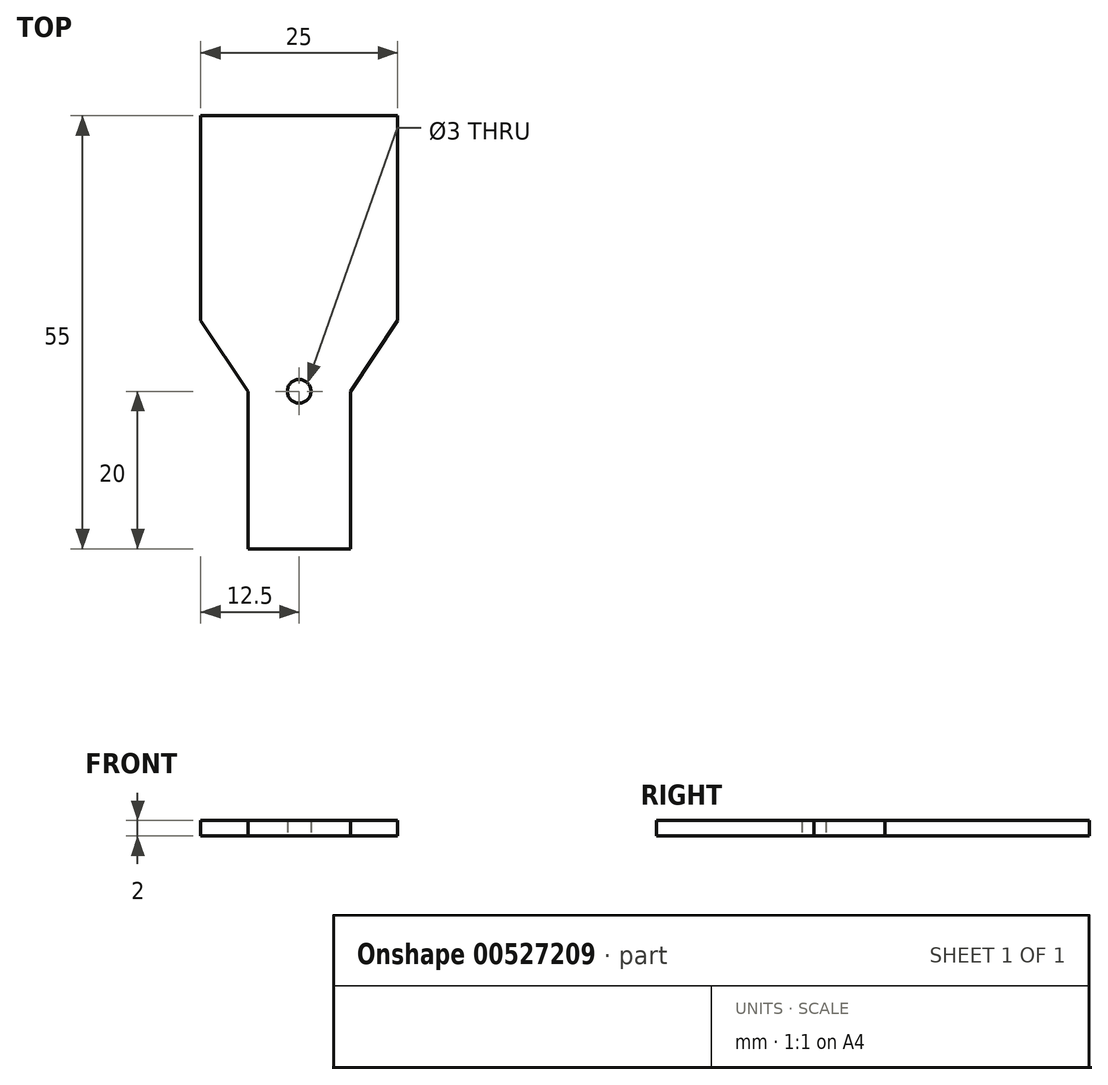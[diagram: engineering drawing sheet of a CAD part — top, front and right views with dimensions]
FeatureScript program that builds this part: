
annotation { "Feature Type Name" : "Feature", "Feature Type Description" : "" }
export const myFeature = defineFeature(function(context is Context, id is Id, definition is map)
    precondition{}
    {
        {
            var Q0;
            Q0=qCreatedBy(makeId("Top.planeOp"),FACE);
            var sketch = newSketch(context, id + "F0", { "sketchPlane" : qUnion([Q0])});
            skLineSegment(sketch, "E0.bottom", {"start": v(-12.5, 35) * mm, "end": v(12.5, 35) * mm});
            skLineSegment(sketch, "E0.top", {"start": v(-12.5, 9) * mm, "end": v(12.5, 9) * mm});
            skLineSegment(sketch, "E0.left", {"start": v(-12.5, 35) * mm, "end": v(-12.5, 9) * mm});
            skLineSegment(sketch, "E0.right", {"start": v(12.5, 35) * mm, "end": v(12.5, 9) * mm});
            skPoint(sketch, "E1", {"position": v(0, 35) * mm});
            skLineSegment(sketch, "E2", {"start": v(0, 35) * mm, "end": v(0, 0) * mm, "construction": true});
            skLineSegment(sketch, "E3", {"start": v(6.5, 0) * mm, "end": v(12.5, 9) * mm});
            skPoint(sketch, "E4", {"position": v(0, 9) * mm});
            skLineSegment(sketch, "E5", {"start": v(0, 9) * mm, "end": v(0, 0) * mm});
            skPoint(sketch, "E6", {"position": v(0, 4.5) * mm});
            skCircle(sketch, "E7", {"center": v(0, 0) * mm, "radius": 6.5 * mm});
            skLineSegment(sketch, "E8.bottom", {"start": v(-6.5, 0) * mm, "end": v(6.5, 0) * mm});
            skLineSegment(sketch, "E8.top", {"start": v(-6.5, -20) * mm, "end": v(6.5, -20) * mm});
            skLineSegment(sketch, "E8.left", {"start": v(-6.5, 0) * mm, "end": v(-6.5, -20) * mm});
            skLineSegment(sketch, "E8.right", {"start": v(6.5, 0) * mm, "end": v(6.5, -20) * mm});
            skLineSegment(sketch, "E9", {"start": v(-6.5, 0) * mm, "end": v(-12.5, 9) * mm});
            skCircle(sketch, "E10", {"center": v(0, 0) * mm, "radius": 1.5 * mm});
            skSolve(sketch);
        }
        {
            var Q0;
            Q0 = qSketchRegion(id + "F0", true);
            extrude(context, id + "F1", {"entities" : qUnion([Q0]), "depth" : 2 * mm, "offsetDistance" : 25 * mm});
        }
    });
